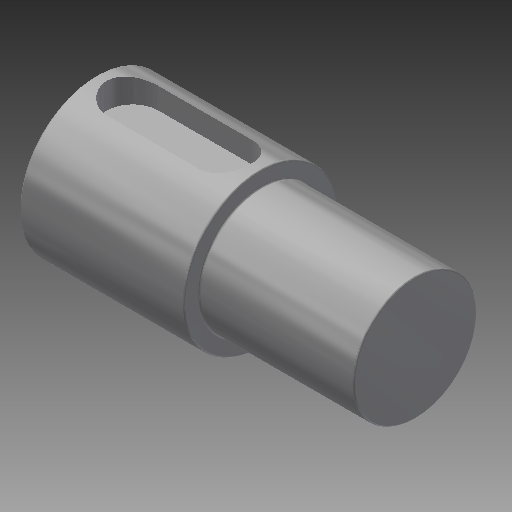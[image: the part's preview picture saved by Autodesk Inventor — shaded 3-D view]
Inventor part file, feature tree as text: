
AUTODESK INVENTOR PART (.ipt)
format: ipt  version: 2019.4 (Build 234330000, 330)  size: 198,656 bytes
history: native  units: mm
features: other x8, fillet x4
ambient origin geometry x6: Origin, XZ Plane, XY Plane, X Axis, Y Axis, Z Axis
bodies: Body1 (feature_tree)
feature tree (12):
  other  "實體1"
  other  "迴轉1"
  other  "鍵槽2"
  fillet  "圓角5"  [1 undecoded]
  other  "鍵槽1"
  fillet  "圓角2"  Radius=15.0mm
  fillet  "圓角3"  Radius=12.0mm
  fillet  "圓角4"  [1 undecoded]
  other  "起始平面"
  other  "主要草圖"
  other  "iFeature3:1"
  other  "iFeature3:2"
note: 2 required parameter values undecoded (feature->parameter linkage not recoverable at this tier; creation-order binding heuristic only, values carry confidence <= 0.55)
